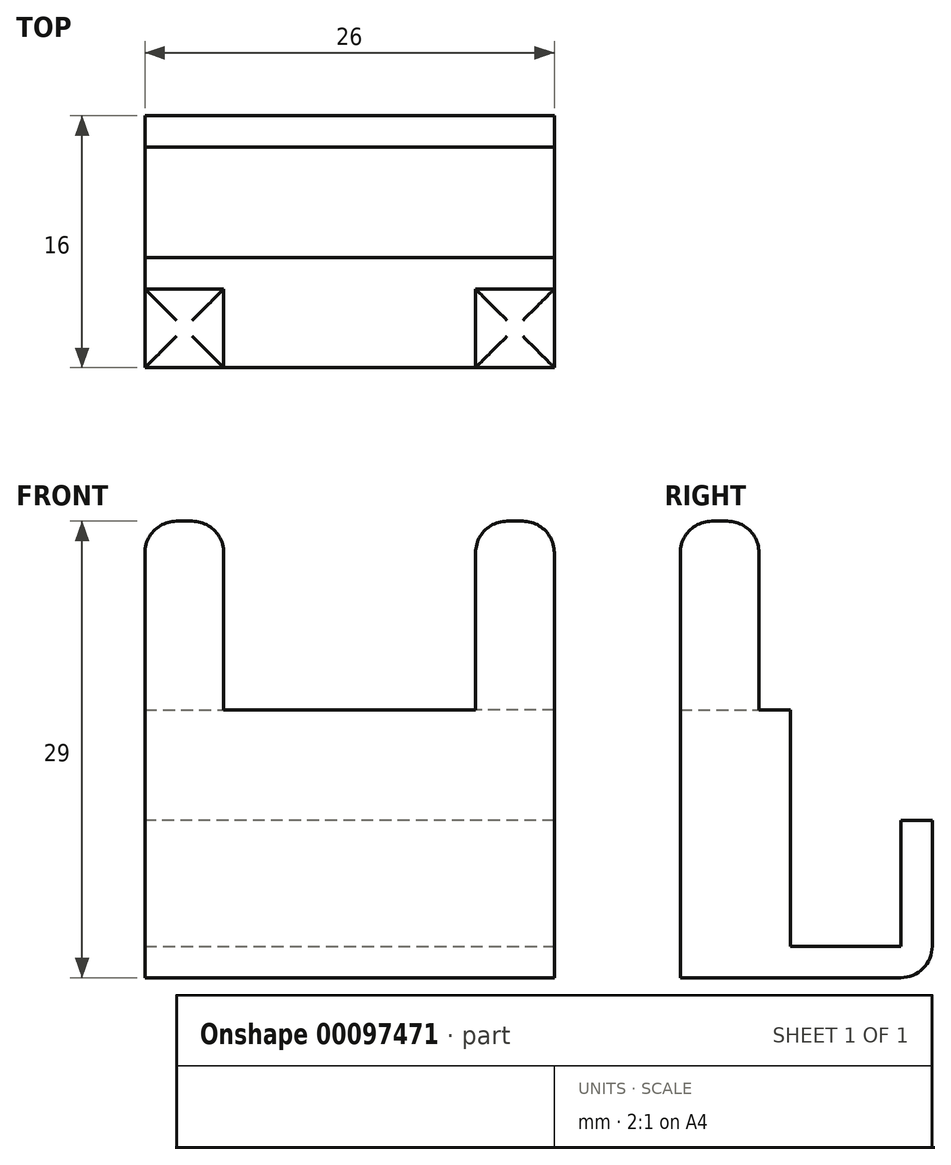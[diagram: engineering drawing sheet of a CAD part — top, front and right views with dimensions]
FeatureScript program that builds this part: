
annotation { "Feature Type Name" : "Feature", "Feature Type Description" : "" }
export const myFeature = defineFeature(function(context is Context, id is Id, definition is map)
    precondition{}
    {
        {
            var Q0;
            Q0=qCreatedBy(makeId("Top.planeOp"),FACE);
            var sketch = newSketch(context, id + "F0", { "sketchPlane" : qUnion([Q0])});
            skLineSegment(sketch, "E0.bottom", {"start": v(0, 0) * mm, "end": v(-26, 0) * mm});
            skLineSegment(sketch, "E0.top", {"start": v(0, 16) * mm, "end": v(-26, 16) * mm});
            skLineSegment(sketch, "E0.left", {"start": v(0, 0) * mm, "end": v(0, 16) * mm});
            skLineSegment(sketch, "E0.right", {"start": v(-26, 0) * mm, "end": v(-26, 16) * mm});
            skSolve(sketch);
        }
        {
            var Q0;
            Q0=makeQuery(id+"F0.imprint","IMPRINT",FACE,{"disambiguationData":[TD([[makeQuery(id+"F0.imprint","IMPRINT",EDGE,{"derivedFrom":sQuery(id+"F0.wireOp",EDGE,"E0.bottom")}),-1.0]])]});
            extrude(context, id + "F1", {"entities" : qUnion([Q0]), "depth" : 2 * mm});
        }
        {
            var Q0;
            Q0=makeQuery(id+"F1.opExtrude","CAP_FACE",FACE,{"disambiguationData":[OSD([sQuery(id+"F0.wireOp",EDGE,"E0.bottom"),sQuery(id+"F0.wireOp",EDGE,"E0.top"),sQuery(id+"F0.wireOp",EDGE,"E0.left"),sQuery(id+"F0.wireOp",EDGE,"E0.right")])],"isStart":false});
            var sketch = newSketch(context, id + "F2", { "sketchPlane" : qUnion([Q0])});
            skLineSegment(sketch, "E1", {"start": v(-26, 7) * mm, "end": v(0, 7) * mm});
            skLineSegment(sketch, "E2", {"start": v(-26, 14) * mm, "end": v(0, 14) * mm});
            skSolve(sketch);
        }
        {
            var Q0;
            {var subQ0=sQuery(id+"F2.wireOp",EDGE,"E1");Q0=makeQuery(id+"F2.imprint","IMPRINT",FACE,{"disambiguationData":[TD([[makeQuery(id+"F2.imprint","IMPRINT",EDGE,{"derivedFrom":subQ0}),-1.0]])]});}
            extrude(context, id + "F3", {"entities" : qUnion([Q0]), "operationType" : NewBodyOperationType.ADD, "depth" : 15 * mm});
        }
        {
            var Q0;
            {var subQ0=sQuery(id+"F2.wireOp",EDGE,"E2");Q0=makeQuery(id+"F2.imprint","IMPRINT",FACE,{"disambiguationData":[TD([[makeQuery(id+"F2.imprint","IMPRINT",EDGE,{"derivedFrom":subQ0}),1.0]])]});}
            extrude(context, id + "F4", {"entities" : qUnion([Q0]), "operationType" : NewBodyOperationType.ADD, "depth" : 8 * mm});
        }
        {
            var Q0;
            Q0=makeQuery(id+"F3.opExtrude","CAP_FACE",FACE,{"disambiguationData":[OSD([sQuery(id+"F0.wireOp",EDGE,"E0.bottom"),sQuery(id+"F0.wireOp",EDGE,"E0.left"),sQuery(id+"F0.wireOp",EDGE,"E0.right"),sQuery(id+"F2.wireOp",EDGE,"E1")])],"isStart":false});
            var sketch = newSketch(context, id + "F5", { "sketchPlane" : qUnion([Q0])});
            skLineSegment(sketch, "E3.bottom", {"start": v(-26, 0) * mm, "end": v(-21, 0) * mm});
            skLineSegment(sketch, "E3.top", {"start": v(-26, 5) * mm, "end": v(-21, 5) * mm});
            skLineSegment(sketch, "E3.left", {"start": v(-26, 0) * mm, "end": v(-26, 5) * mm});
            skLineSegment(sketch, "E3.right", {"start": v(-21, 0) * mm, "end": v(-21, 5) * mm});
            skLineSegment(sketch, "E4.bottom", {"start": v(0, 0) * mm, "end": v(-5, 0) * mm});
            skLineSegment(sketch, "E4.top", {"start": v(0, 5) * mm, "end": v(-5, 5) * mm});
            skLineSegment(sketch, "E4.left", {"start": v(0, 0) * mm, "end": v(0, 5) * mm});
            skLineSegment(sketch, "E4.right", {"start": v(-5, 0) * mm, "end": v(-5, 5) * mm});
            skSolve(sketch);
        }
        {
            var Q0;
            Q0=makeQuery(id+"F5.imprint","IMPRINT",FACE,{"disambiguationData":[TD([[makeQuery(id+"F5.imprint","IMPRINT",EDGE,{"derivedFrom":sQuery(id+"F5.wireOp",EDGE,"E3.bottom")}),1.0]])]});
            var Q1;
            Q1=makeQuery(id+"F5.imprint","IMPRINT",FACE,{"disambiguationData":[TD([[makeQuery(id+"F5.imprint","IMPRINT",EDGE,{"derivedFrom":sQuery(id+"F5.wireOp",EDGE,"E4.bottom")}),-1.0]])]});
            var Q2;
            Q2=makeQuery(id+"F5.imprint","IMPRINT",FACE,{"disambiguationData":[TD([[makeQuery(id+"F5.imprint","IMPRINT",EDGE,{"derivedFrom":sQuery(id+"F5.wireOp",EDGE,"E3.bottom")}),-1.0]])]});
            extrude(context, id + "F6", {"entities" : qUnion([Q0, Q1, Q2]), "operationType" : NewBodyOperationType.ADD, "depth" : 12 * mm});
        }
        {
            var Q0;
            Q0=makeQuery(id+"F1.opExtrude","CAP_EDGE",EDGE,{"disambiguationData":[OSD([sQuery(id+"F0.wireOp",EDGE,"E0.top")])],"isStart":true});
            fillet(context, id + "F7", {"entities" : qUnion([Q0]), "radius" : 2 * mm, "tangentPropagation" : true, "allowEdgeOverflow" : false});
        }
        {
            var Q0;
            Q0=makeQuery(id+"F6.opExtrude","CAP_FACE",FACE,{"disambiguationData":[OSD([sQuery(id+"F5.wireOp",EDGE,"E3.bottom"),sQuery(id+"F5.wireOp",EDGE,"E3.top"),sQuery(id+"F5.wireOp",EDGE,"E3.left"),sQuery(id+"F5.wireOp",EDGE,"E3.right")])],"isStart":false});
            var Q1;
            Q1=makeQuery(id+"F6.opExtrude","CAP_FACE",FACE,{"disambiguationData":[OSD([sQuery(id+"F5.wireOp",EDGE,"E4.bottom"),sQuery(id+"F5.wireOp",EDGE,"E4.top"),sQuery(id+"F5.wireOp",EDGE,"E4.left"),sQuery(id+"F5.wireOp",EDGE,"E4.right")])],"isStart":false});
            fillet(context, id + "F8", {"entities" : qUnion([Q0, Q1]), "radius" : 2 * mm, "tangentPropagation" : true, "allowEdgeOverflow" : false});
        }
    });
